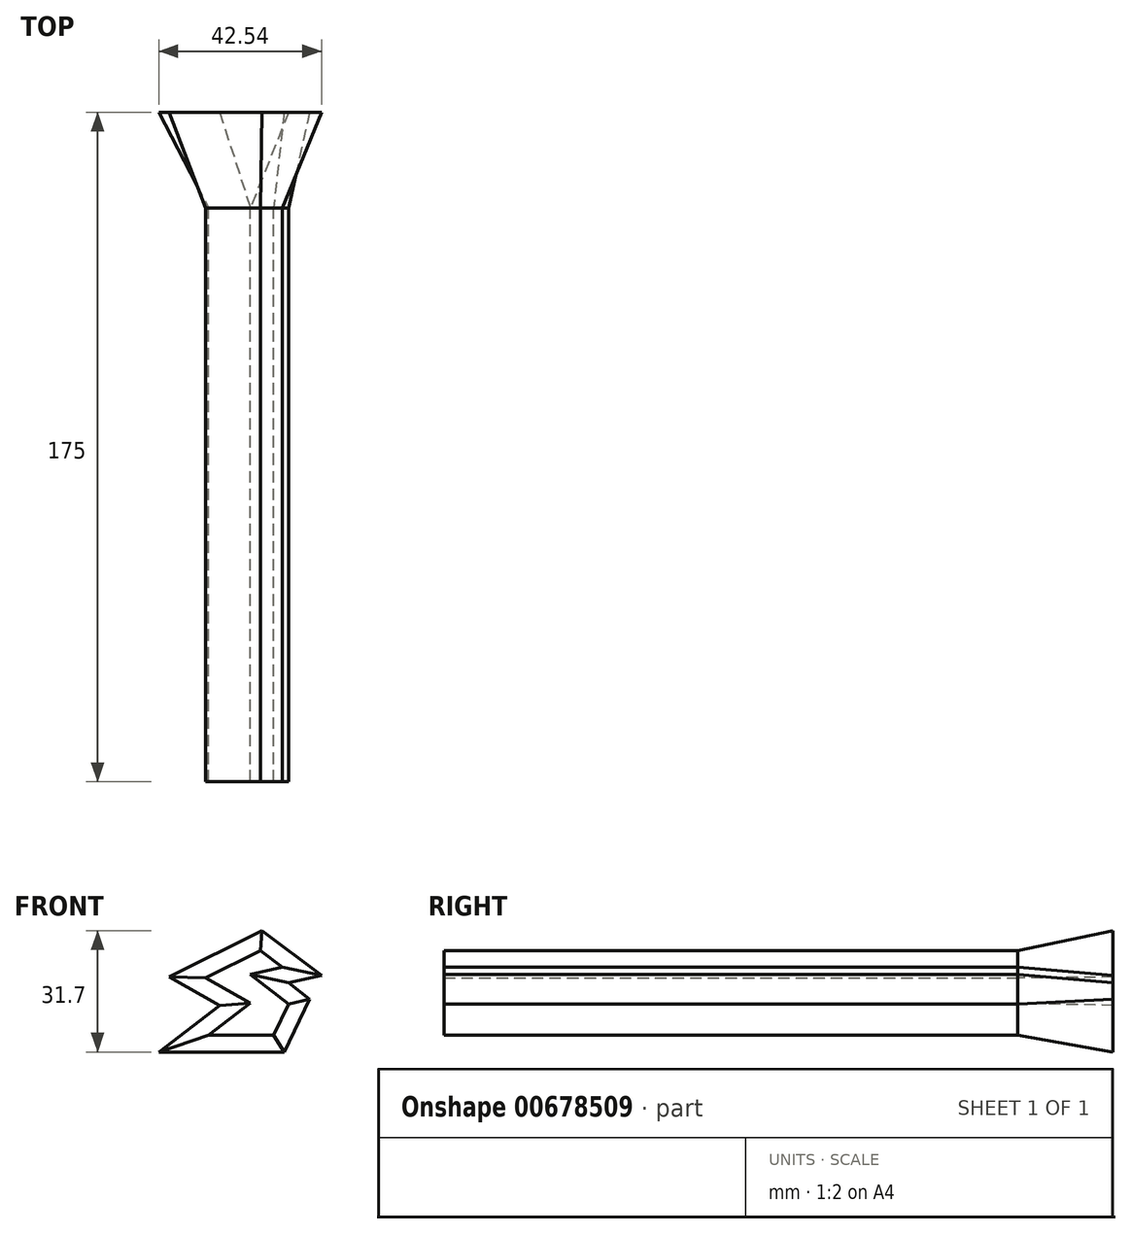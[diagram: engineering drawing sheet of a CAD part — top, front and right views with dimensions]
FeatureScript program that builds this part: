
annotation { "Feature Type Name" : "Feature", "Feature Type Description" : "" }
export const myFeature = defineFeature(function(context is Context, id is Id, definition is map)
    precondition{}
    {
        {
            var Q0;
            Q0=qCreatedBy(makeId("Front.planeOp"),FACE);
            var sketch = newSketch(context, id + "F0", { "sketchPlane" : qUnion([Q0])});
            skLineSegment(sketch, "E0", {"start": v(42.1, -21.12) * mm, "end": v(27.73, -28.3) * mm});
            skLineSegment(sketch, "E1", {"start": v(27.73, -28.3) * mm, "end": v(39.52, -34.92) * mm});
            skLineSegment(sketch, "E2", {"start": v(47.85, -25.44) * mm, "end": v(42.1, -21.12) * mm});
            skLineSegment(sketch, "E3", {"start": v(45.6, -43.26) * mm, "end": v(49.48, -35.17) * mm});
            skLineSegment(sketch, "E4", {"start": v(49.48, -35.17) * mm, "end": v(39.52, -27.35) * mm});
            skLineSegment(sketch, "E5", {"start": v(39.52, -27.35) * mm, "end": v(47.85, -25.44) * mm});
            skLineSegment(sketch, "E6", {"start": v(39.52, -34.92) * mm, "end": v(28.6, -43.26) * mm});
            skLineSegment(sketch, "E7", {"start": v(28.6, -43.26) * mm, "end": v(45.6, -43.26) * mm});
            skSolve(sketch);
        }
        {
            var Q0;
            Q0=makeQuery(id+"F0.imprint","IMPRINT",FACE,{"disambiguationData":[TD([[makeQuery(id+"F0.imprint","IMPRINT",EDGE,{"derivedFrom":sQuery(id+"F0.wireOp",EDGE,"E0")}),1.0]])]});
            extrude(context, id + "F1", {"entities" : qUnion([Q0]), "depth" : 150 * mm, "offsetDistance" : 25 * mm});
        }
        {
            var Q0;
            Q0=makeQuery(id+"F1.opExtrude","CAP_FACE",FACE,{"disambiguationData":[OSD([sQuery(id+"F0.wireOp",EDGE,"E0"),sQuery(id+"F0.wireOp",EDGE,"E1"),sQuery(id+"F0.wireOp",EDGE,"YfmAGRTc-UG7Z-Ft5F-Ta1N-NRtwnuUKnnU7"),sQuery(id+"F0.wireOp",EDGE,"rT2lIosg-NJrZ-VrbR-GnI0-06fzHHVl0ixb"),sQuery(id+"F0.wireOp",EDGE,"Kz4qNhzu-5a5F-2FZe-oTmN-Ux5WzvpXfRvz"),sQuery(id+"F0.wireOp",EDGE,"0DOUoCsz-ltk4-cOZ1-AmXy-67cdAQDOcEE5"),sQuery(id+"F0.wireOp",EDGE,"AiCMZWPP-gkjD-6bYG-W74t-s4Q7StxEG3Um"),sQuery(id+"F0.wireOp",EDGE,"E2")])],"isStart":true});
            extrude(context, id + "F2", {"entities" : qUnion([Q0]), "operationType" : NewBodyOperationType.ADD, "depth" : 25 * mm, "offsetDistance" : 25 * mm, "hasDraft" : true, "draftAngle" : 10 * degree});
        }
    });
